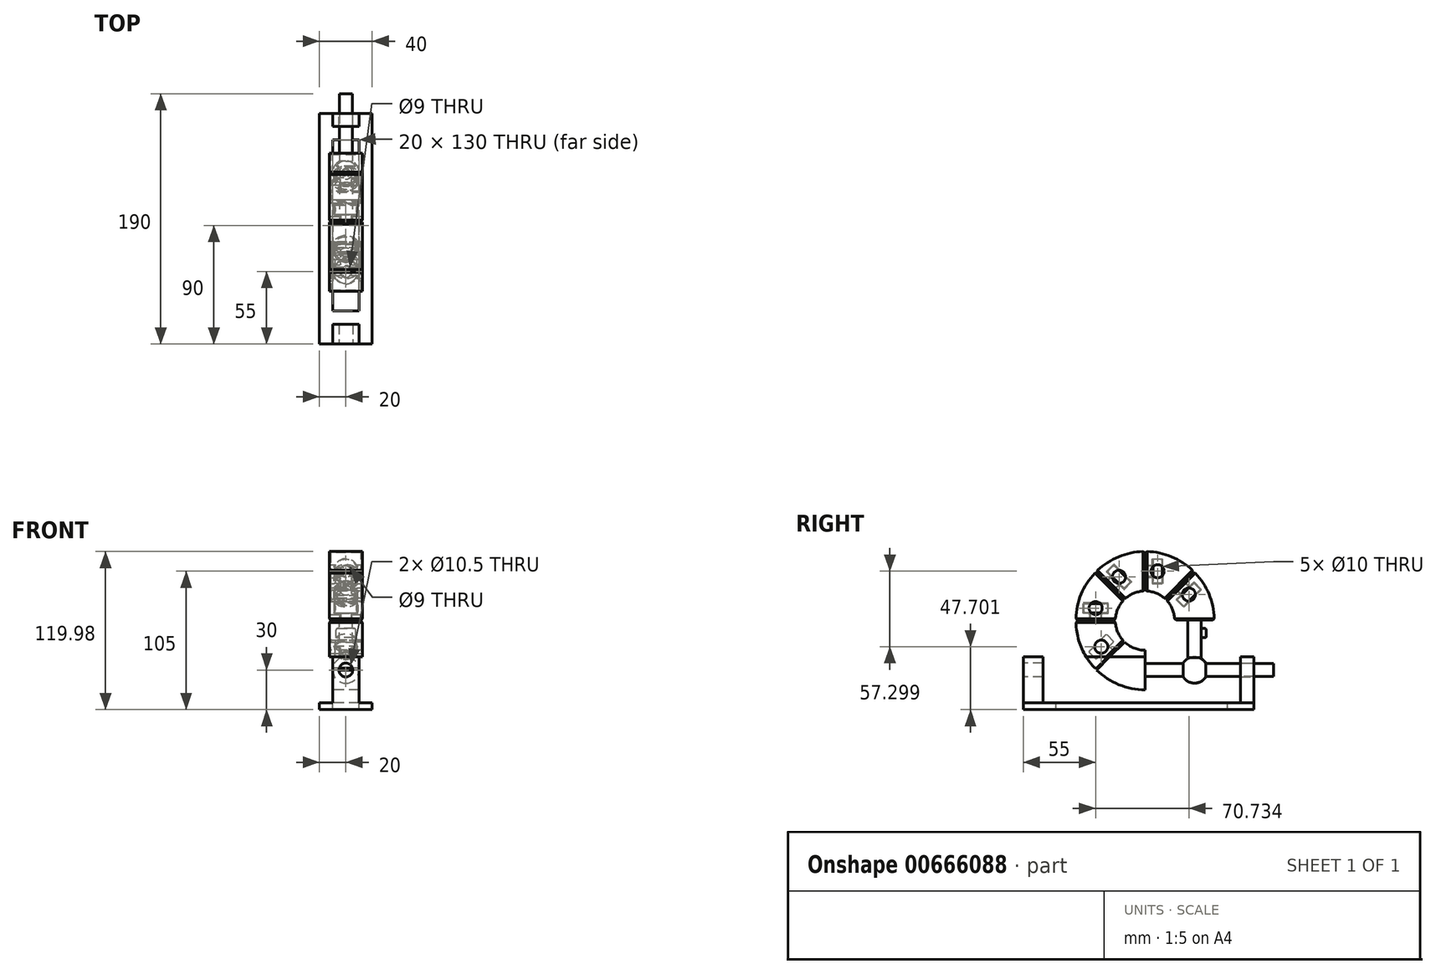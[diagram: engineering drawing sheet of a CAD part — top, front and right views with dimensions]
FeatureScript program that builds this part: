
annotation { "Feature Type Name" : "Feature", "Feature Type Description" : "" }
export const myFeature = defineFeature(function(context is Context, id is Id, definition is map)
    precondition{}
    {
        {
            var Q0;
            Q0=qCreatedBy(makeId("Right.planeOp"),FACE);
            var sketch = newSketch(context, id + "F0", { "sketchPlane" : qUnion([Q0])});
            skLineSegment(sketch, "E0", {"start": v(0, 30) * mm, "end": v(0, 0) * mm});
            skArc(sketch, "E1", {"start": v(-37.12, 15.38) * mm, "mid": v(-20.1, 4) * mm, "end": v(0, 0) * mm});
            skArc(sketch, "E2", {"start": v(0, 30) * mm, "mid": v(-8.61, 31.71) * mm, "end": v(-15.9, 36.6) * mm});
            skLineSegment(sketch, "E3", {"start": v(-15.9, 36.6) * mm, "end": v(-37.12, 15.38) * mm, "construction": true});
            skLineSegment(sketch, "E4", {"start": v(-23.33, 28.46) * mm, "end": v(-27.93, 33.05) * mm});
            skLineSegment(sketch, "E5", {"start": v(-33.59, 27.4) * mm, "end": v(-29, 22.8) * mm});
            skLineSegment(sketch, "E6", {"start": v(-33.59, 27.4) * mm, "end": v(-36.42, 24.57) * mm});
            skLineSegment(sketch, "E7", {"start": v(-37.83, 24.57) * mm, "end": v(-41.37, 28.1) * mm});
            skLineSegment(sketch, "E8", {"start": v(-41.37, 29.52) * mm, "end": v(-30.05, 40.83) * mm});
            skLineSegment(sketch, "E9", {"start": v(-28.64, 40.83) * mm, "end": v(-25.1, 37.3) * mm});
            skLineSegment(sketch, "E10", {"start": v(-25.1, 35.88) * mm, "end": v(-27.93, 33.05) * mm});
            skLineSegment(sketch, "E11", {"start": v(-26.52, 25.98) * mm, "end": v(-36.06, 35.53) * mm});
            skArc(sketch, "E12.MirrorCS", {"start": v(-22.5, 52.5) * mm, "mid": v(-20.79, 43.89) * mm, "end": v(-15.9, 36.6) * mm});
            skLineSegment(sketch, "E13.MirrorCS", {"start": v(-22.5, 52.5) * mm, "end": v(-52.5, 52.5) * mm});
            skArc(sketch, "E14.MirrorCS", {"start": v(-37.12, 15.38) * mm, "mid": v(-48.5, 32.4) * mm, "end": v(-52.5, 52.5) * mm});
            skLineSegment(sketch, "E15", {"start": v(-16.26, 36.95) * mm, "end": v(-22.98, 30.23) * mm});
            skLineSegment(sketch, "E16.MirrorCS", {"start": v(-37.48, 15.73) * mm, "end": v(-30.76, 22.45) * mm});
            skLineSegment(sketch, "E17", {"start": v(-36.77, 15.02) * mm, "end": v(-15.55, 36.24) * mm});
            skLineSegment(sketch, "E18", {"start": v(-30.76, 23.86) * mm, "end": v(-32.88, 25.98) * mm});
            skLineSegment(sketch, "E19", {"start": v(-34.3, 25.98) * mm, "end": v(-37.12, 23.16) * mm});
            skLineSegment(sketch, "E20", {"start": v(-37.12, 23.16) * mm, "end": v(-42.78, 28.81) * mm});
            skLineSegment(sketch, "E21", {"start": v(-42.78, 28.81) * mm, "end": v(-29.34, 42.25) * mm});
            skLineSegment(sketch, "E22", {"start": v(-29.34, 42.25) * mm, "end": v(-23.69, 36.6) * mm});
            skLineSegment(sketch, "E23", {"start": v(-23.69, 36.6) * mm, "end": v(-26.52, 33.76) * mm});
            skLineSegment(sketch, "E24", {"start": v(-26.52, 32.35) * mm, "end": v(-24.4, 30.23) * mm});
            skLineSegment(sketch, "E25", {"start": v(0, 52.5) * mm, "end": v(-51.67, 31.1) * mm, "construction": true});
            skArc(sketch, "E26.1.21", {"start": v(-16.26, 36.95) * mm, "mid": v(-20.88, 44.12) * mm, "end": v(-22.5, 52.5) * mm});
            skPoint(sketch, "E27.orphan", {"position": v(-23.69, 28.81) * mm});
            skPoint(sketch, "E28.orphan", {"position": v(-29.34, 23.16) * mm});
            skLineSegment(sketch, "E29.1.0", {"start": v(-42, 54) * mm, "end": v(-42, 57) * mm});
            skLineSegment(sketch, "E29.1.1", {"start": v(-43, 58) * mm, "end": v(-47, 58) * mm});
            skLineSegment(sketch, "E29.1.2", {"start": v(-47, 58) * mm, "end": v(-47, 66) * mm});
            skLineSegment(sketch, "E29.1.3", {"start": v(-47, 66) * mm, "end": v(-28, 66) * mm});
            skLineSegment(sketch, "E29.1.4", {"start": v(-28, 66) * mm, "end": v(-28, 58) * mm});
            skLineSegment(sketch, "E29.1.5", {"start": v(-28, 58) * mm, "end": v(-32, 58) * mm});
            skLineSegment(sketch, "E29.1.6", {"start": v(-33, 57) * mm, "end": v(-33, 54) * mm});
            skLineSegment(sketch, "E29.1.7", {"start": v(-22.5, 53) * mm, "end": v(-32, 53) * mm});
            skLineSegment(sketch, "E29.1.8", {"start": v(-52.5, 53) * mm, "end": v(-43, 53) * mm});
            skArc(sketch, "E29.1.9", {"start": v(-52.5, 52.5) * mm, "mid": v(-48.5, 72.6) * mm, "end": v(-37.12, 89.62) * mm});
            skArc(sketch, "E29.1.10", {"start": v(-22.5, 53) * mm, "mid": v(-20.7, 61.34) * mm, "end": v(-15.9, 68.4) * mm});
            skLineSegment(sketch, "E29.1.11", {"start": v(-52.5, 52) * mm, "end": v(-22.5, 52) * mm});
            skLineSegment(sketch, "E29.1.12", {"start": v(-15.9, 68.4) * mm, "end": v(-37.12, 89.62) * mm});
            skLineSegment(sketch, "E29.1.13", {"start": v(-28.5, 64.5) * mm, "end": v(-28.5, 59.5) * mm});
            skLineSegment(sketch, "E29.1.14", {"start": v(-45.5, 65.5) * mm, "end": v(-29.5, 65.5) * mm});
            skLineSegment(sketch, "E29.1.15", {"start": v(-46.5, 59.5) * mm, "end": v(-46.5, 64.5) * mm});
            skLineSegment(sketch, "E29.1.16", {"start": v(-41.5, 58.5) * mm, "end": v(-45.5, 58.5) * mm});
            skLineSegment(sketch, "E29.1.17", {"start": v(-41.5, 58.5) * mm, "end": v(-41.5, 52) * mm});
            skLineSegment(sketch, "E29.1.18", {"start": v(-33.5, 52) * mm, "end": v(-33.5, 58.5) * mm});
            skLineSegment(sketch, "E29.1.19", {"start": v(-29.5, 58.5) * mm, "end": v(-33.5, 58.5) * mm});
            skLineSegment(sketch, "E29.2.0", {"start": v(-29.34, 82.55) * mm, "end": v(-25.8, 86.09) * mm});
            skLineSegment(sketch, "E29.2.1", {"start": v(-25.8, 86.09) * mm, "end": v(-29.34, 89.62) * mm});
            skLineSegment(sketch, "E29.2.2", {"start": v(-29.34, 89.62) * mm, "end": v(-23.69, 95.28) * mm});
            skLineSegment(sketch, "E29.2.3", {"start": v(-23.69, 95.28) * mm, "end": v(-10.25, 81.84) * mm});
            skLineSegment(sketch, "E29.2.4", {"start": v(-10.25, 81.84) * mm, "end": v(-15.9, 76.19) * mm});
            skLineSegment(sketch, "E29.2.5", {"start": v(-15.9, 76.19) * mm, "end": v(-19.45, 79.72) * mm});
            skLineSegment(sketch, "E29.2.6", {"start": v(-19.45, 79.72) * mm, "end": v(-22.98, 76.19) * mm});
            skLineSegment(sketch, "E29.2.7", {"start": v(-15.55, 68.76) * mm, "end": v(-22.98, 76.19) * mm});
            skLineSegment(sketch, "E29.2.8", {"start": v(-36.77, 89.98) * mm, "end": v(-29.34, 82.55) * mm});
            skArc(sketch, "E29.2.9", {"start": v(-37.12, 89.62) * mm, "mid": v(-20.1, 101) * mm, "end": v(0, 105) * mm});
            skArc(sketch, "E29.2.10", {"start": v(-15.55, 68.76) * mm, "mid": v(-8.38, 73.38) * mm, "end": v(0, 75) * mm});
            skLineSegment(sketch, "E29.2.11", {"start": v(-37.48, 89.27) * mm, "end": v(-16.26, 68.05) * mm});
            skLineSegment(sketch, "E29.2.12", {"start": v(0, 75) * mm, "end": v(0, 105) * mm});
            skLineSegment(sketch, "E29.2.13", {"start": v(-10.96, 81.84) * mm, "end": v(-15.9, 76.9) * mm});
            skLineSegment(sketch, "E29.2.14", {"start": v(-23.69, 94.57) * mm, "end": v(-10.96, 81.84) * mm});
            skLineSegment(sketch, "E29.2.15", {"start": v(-28.64, 89.62) * mm, "end": v(-23.69, 94.57) * mm});
            skLineSegment(sketch, "E29.2.16", {"start": v(-25.1, 86.09) * mm, "end": v(-28.64, 89.62) * mm});
            skLineSegment(sketch, "E29.2.17", {"start": v(-25.1, 86.09) * mm, "end": v(-29.7, 81.5) * mm});
            skLineSegment(sketch, "E29.2.18", {"start": v(-24.04, 75.83) * mm, "end": v(-19.45, 80.43) * mm});
            skLineSegment(sketch, "E29.2.19", {"start": v(-15.9, 76.9) * mm, "end": v(-19.45, 80.43) * mm});
            skLineSegment(sketch, "E29.3.0", {"start": v(0.5, 94.5) * mm, "end": v(5.5, 94.5) * mm});
            skLineSegment(sketch, "E29.3.1", {"start": v(5.5, 94.5) * mm, "end": v(5.5, 99.5) * mm});
            skLineSegment(sketch, "E29.3.2", {"start": v(5.5, 99.5) * mm, "end": v(13.5, 99.5) * mm});
            skLineSegment(sketch, "E29.3.3", {"start": v(13.5, 99.5) * mm, "end": v(13.5, 80.5) * mm});
            skLineSegment(sketch, "E29.3.4", {"start": v(13.5, 80.5) * mm, "end": v(5.5, 80.5) * mm});
            skLineSegment(sketch, "E29.3.5", {"start": v(5.5, 80.5) * mm, "end": v(5.5, 85.5) * mm});
            skLineSegment(sketch, "E29.3.6", {"start": v(5.5, 85.5) * mm, "end": v(0.5, 85.5) * mm});
            skLineSegment(sketch, "E29.3.7", {"start": v(0.5, 75) * mm, "end": v(0.5, 85.5) * mm});
            skLineSegment(sketch, "E29.3.8", {"start": v(0.5, 105) * mm, "end": v(0.5, 94.5) * mm});
            skArc(sketch, "E29.3.9", {"start": v(0, 105) * mm, "mid": v(20.1, 101) * mm, "end": v(37.12, 89.62) * mm});
            skArc(sketch, "E29.3.10", {"start": v(0.5, 75) * mm, "mid": v(8.84, 73.2) * mm, "end": v(15.9, 68.4) * mm});
            skLineSegment(sketch, "E29.3.11", {"start": v(-0.5, 105) * mm, "end": v(-0.5, 75) * mm});
            skLineSegment(sketch, "E29.3.12", {"start": v(15.9, 68.4) * mm, "end": v(37.12, 89.62) * mm});
            skLineSegment(sketch, "E29.3.13", {"start": v(13, 81) * mm, "end": v(6, 81) * mm});
            skLineSegment(sketch, "E29.3.14", {"start": v(13, 99) * mm, "end": v(13, 81) * mm});
            skLineSegment(sketch, "E29.3.15", {"start": v(6, 99) * mm, "end": v(13, 99) * mm});
            skLineSegment(sketch, "E29.3.16", {"start": v(6, 94) * mm, "end": v(6, 99) * mm});
            skLineSegment(sketch, "E29.3.17", {"start": v(6, 94) * mm, "end": v(-0.5, 94) * mm});
            skLineSegment(sketch, "E29.3.18", {"start": v(-0.5, 86) * mm, "end": v(6, 86) * mm});
            skLineSegment(sketch, "E29.3.19", {"start": v(6, 81) * mm, "end": v(6, 86) * mm});
            skLineSegment(sketch, "E29.4.0", {"start": v(30.05, 81.84) * mm, "end": v(33.59, 78.3) * mm});
            skLineSegment(sketch, "E29.4.1", {"start": v(33.59, 78.3) * mm, "end": v(37.12, 81.84) * mm});
            skLineSegment(sketch, "E29.4.2", {"start": v(37.12, 81.84) * mm, "end": v(42.78, 76.19) * mm});
            skLineSegment(sketch, "E29.4.3", {"start": v(42.78, 76.19) * mm, "end": v(29.34, 62.75) * mm});
            skLineSegment(sketch, "E29.4.4", {"start": v(29.34, 62.75) * mm, "end": v(23.69, 68.4) * mm});
            skLineSegment(sketch, "E29.4.5", {"start": v(23.69, 68.4) * mm, "end": v(27.22, 71.95) * mm});
            skLineSegment(sketch, "E29.4.6", {"start": v(27.22, 71.95) * mm, "end": v(23.69, 75.48) * mm});
            skLineSegment(sketch, "E29.4.7", {"start": v(16.26, 68.05) * mm, "end": v(23.69, 75.48) * mm});
            skLineSegment(sketch, "E29.4.8", {"start": v(37.48, 89.27) * mm, "end": v(30.05, 81.84) * mm});
            skArc(sketch, "E29.4.9", {"start": v(37.12, 89.62) * mm, "mid": v(48.5, 72.6) * mm, "end": v(52.5, 52.5) * mm});
            skArc(sketch, "E29.4.10", {"start": v(16.26, 68.05) * mm, "mid": v(20.88, 60.88) * mm, "end": v(22.5, 52.5) * mm});
            skLineSegment(sketch, "E29.4.11", {"start": v(36.77, 89.98) * mm, "end": v(15.55, 68.76) * mm});
            skLineSegment(sketch, "E29.4.12", {"start": v(22.5, 52.5) * mm, "end": v(52.5, 52.5) * mm});
            skLineSegment(sketch, "E29.4.13", {"start": v(29.34, 63.46) * mm, "end": v(24.4, 68.4) * mm});
            skLineSegment(sketch, "E29.4.14", {"start": v(42.07, 76.19) * mm, "end": v(29.34, 63.46) * mm});
            skLineSegment(sketch, "E29.4.15", {"start": v(37.12, 81.14) * mm, "end": v(42.07, 76.19) * mm});
            skLineSegment(sketch, "E29.4.16", {"start": v(33.59, 77.6) * mm, "end": v(37.12, 81.14) * mm});
            skLineSegment(sketch, "E29.4.17", {"start": v(33.59, 77.6) * mm, "end": v(29, 82.2) * mm});
            skLineSegment(sketch, "E29.4.18", {"start": v(23.33, 76.54) * mm, "end": v(27.93, 71.95) * mm});
            skLineSegment(sketch, "E29.4.19", {"start": v(24.4, 68.4) * mm, "end": v(27.93, 71.95) * mm});
            skLineSegment(sketch, "E29.anchor1", {"start": v(0, 52.5) * mm, "end": v(-33.59, 26.7) * mm, "construction": true});
            skLineSegment(sketch, "E29.anchor2", {"start": v(0, 52.5) * mm, "end": v(33.59, 78.3) * mm, "construction": true});
            skLineSegment(sketch, "E30", {"start": v(0, 20) * mm, "end": v(40, 20) * mm});
            skLineSegment(sketch, "E31", {"start": v(40, 20) * mm, "end": v(40, 10) * mm});
            skLineSegment(sketch, "E32", {"start": v(40, 10) * mm, "end": v(0, 10) * mm});
            skLineSegment(sketch, "E33", {"start": v(32.5, 53) * mm, "end": v(32.5, 25) * mm});
            skLineSegment(sketch, "E34", {"start": v(32.5, 25) * mm, "end": v(42.5, 25) * mm, "construction": true});
            skLineSegment(sketch, "E35", {"start": v(42.5, 25) * mm, "end": v(42.5, 53) * mm});
            skLineSegment(sketch, "E36", {"start": v(0, 15) * mm, "end": v(40, 15) * mm});
            skPoint(sketch, "E36.endSnap0", {"position": v(0, 15) * mm});
            skLineSegment(sketch, "E37", {"start": v(37.5, 53) * mm, "end": v(37.5, 15) * mm});
            skLineSegment(sketch, "E38", {"start": v(-26.52, 25.98) * mm, "end": v(-26.16, 25.63) * mm});
            skLineSegment(sketch, "E39", {"start": v(-24.04, 29.17) * mm, "end": v(-29.7, 23.5) * mm});
            skLineSegment(sketch, "E40", {"start": v(-37.5, 52) * mm, "end": v(-37.5, 65.5) * mm});
            skPoint(sketch, "E41.visualSharp", {"position": v(-42.07, 28.81) * mm});
            skArc(sketch, "E41.filletArc", {"start": v(-41.37, 29.52) * mm, "mid": v(-41.66, 28.81) * mm, "end": v(-41.37, 28.1) * mm});
            skPoint(sketch, "E42.visualSharp", {"position": v(-29.34, 41.54) * mm});
            skArc(sketch, "E42.filletArc", {"start": v(-28.64, 40.83) * mm, "mid": v(-29.34, 41.13) * mm, "end": v(-30.05, 40.83) * mm});
            skPoint(sketch, "E43.visualSharp", {"position": v(-24.4, 36.6) * mm});
            skArc(sketch, "E43.filletArc", {"start": v(-25.1, 35.88) * mm, "mid": v(-24.8, 36.6) * mm, "end": v(-25.1, 37.3) * mm});
            skPoint(sketch, "E44.visualSharp", {"position": v(-37.12, 23.86) * mm});
            skArc(sketch, "E44.filletArc", {"start": v(-37.83, 24.57) * mm, "mid": v(-37.12, 24.28) * mm, "end": v(-36.42, 24.57) * mm});
            skPoint(sketch, "E45.visualSharp", {"position": v(-27.22, 33.05) * mm});
            skArc(sketch, "E45.filletArc", {"start": v(-26.52, 33.76) * mm, "mid": v(-26.8, 33.05) * mm, "end": v(-26.52, 32.35) * mm});
            skPoint(sketch, "E46.visualSharp", {"position": v(-33.59, 26.7) * mm});
            skArc(sketch, "E46.filletArc", {"start": v(-32.88, 25.98) * mm, "mid": v(-33.59, 26.28) * mm, "end": v(-34.3, 25.98) * mm});
            skPoint(sketch, "E47.visualSharp", {"position": v(-46.5, 65.5) * mm});
            skArc(sketch, "E47.filletArc", {"start": v(-45.5, 65.5) * mm, "mid": v(-46.2, 65.2) * mm, "end": v(-46.5, 64.5) * mm});
            skPoint(sketch, "E48.visualSharp", {"position": v(-28.5, 65.5) * mm});
            skArc(sketch, "E48.filletArc", {"start": v(-28.5, 64.5) * mm, "mid": v(-28.8, 65.2) * mm, "end": v(-29.5, 65.5) * mm});
            skPoint(sketch, "E49.visualSharp", {"position": v(-28.5, 58.5) * mm});
            skArc(sketch, "E49.filletArc", {"start": v(-29.5, 58.5) * mm, "mid": v(-28.8, 58.8) * mm, "end": v(-28.5, 59.5) * mm});
            skPoint(sketch, "E50.visualSharp", {"position": v(-33, 58) * mm});
            skArc(sketch, "E50.filletArc", {"start": v(-32, 58) * mm, "mid": v(-32.7, 57.7) * mm, "end": v(-33, 57) * mm});
            skPoint(sketch, "E51.visualSharp", {"position": v(-42, 58) * mm});
            skArc(sketch, "E51.filletArc", {"start": v(-42, 57) * mm, "mid": v(-42.3, 57.7) * mm, "end": v(-43, 58) * mm});
            skPoint(sketch, "E52.visualSharp", {"position": v(-46.5, 58.5) * mm});
            skArc(sketch, "E52.filletArc", {"start": v(-46.5, 59.5) * mm, "mid": v(-46.2, 58.8) * mm, "end": v(-45.5, 58.5) * mm});
            skLineSegment(sketch, "E53", {"start": v(22.5, 53) * mm, "end": v(52.5, 53) * mm});
            skPoint(sketch, "E54.visualSharp", {"position": v(-42, 53) * mm});
            skArc(sketch, "E54.filletArc", {"start": v(-43, 53) * mm, "mid": v(-42.3, 53.3) * mm, "end": v(-42, 54) * mm});
            skPoint(sketch, "E55.visualSharp", {"position": v(-33, 53) * mm});
            skArc(sketch, "E55.filletArc", {"start": v(-33, 54) * mm, "mid": v(-32.7, 53.3) * mm, "end": v(-32, 53) * mm});
            skPoint(sketch, "E56.visualSharp", {"position": v(-30.05, 23.16) * mm});
            skArc(sketch, "E56.filletArc", {"start": v(-30.76, 22.45) * mm, "mid": v(-30.47, 23.16) * mm, "end": v(-30.76, 23.86) * mm});
            skPoint(sketch, "E57.visualSharp", {"position": v(-23.69, 29.52) * mm});
            skArc(sketch, "E57.filletArc", {"start": v(-24.4, 30.23) * mm, "mid": v(-23.69, 29.93) * mm, "end": v(-22.98, 30.23) * mm});
            skLineSegment(sketch, "E58", {"start": v(-30.76, 22.45) * mm, "end": v(-29.7, 23.5) * mm});
            skLineSegment(sketch, "E59", {"start": v(-24.04, 29.17) * mm, "end": v(-22.98, 30.23) * mm});
            skLineSegment(sketch, "E60", {"start": v(42.5, 52.5) * mm, "end": v(52.5, 52.5) * mm});
            skLineSegment(sketch, "E61", {"start": v(0, 20) * mm, "end": v(0, 30) * mm});
            skLineSegment(sketch, "E62", {"start": v(0, 10) * mm, "end": v(0, 0) * mm});
            skLineSegment(sketch, "E63", {"start": v(37.5, 15) * mm, "end": v(40, 15) * mm, "construction": true});
            skArc(sketch, "E64", {"start": v(37.5, 25) * mm, "mid": v(47.5, 15) * mm, "end": v(37.5, 5) * mm});
            skLineSegment(sketch, "E65", {"start": v(37.5, 15) * mm, "end": v(37.5, 5) * mm});
            skLineSegment(sketch, "E66", {"start": v(0, 30) * mm, "end": v(40, 30) * mm});
            skLineSegment(sketch, "E67", {"start": v(40, 30) * mm, "end": v(40, 20) * mm});
            skLineSegment(sketch, "E68", {"start": v(32.5, 25) * mm, "end": v(32.5, 24.5) * mm});
            skLineSegment(sketch, "E69", {"start": v(32.5, 24.5) * mm, "end": v(42.5, 24.5) * mm});
            skLineSegment(sketch, "E70", {"start": v(42.5, 24.5) * mm, "end": v(42.5, 25) * mm});
            skLineSegment(sketch, "E71", {"start": v(52.5, 52.5) * mm, "end": v(52.5, 28.52) * mm});
            skLineSegment(sketch, "E72", {"start": v(52.5, 28.52) * mm, "end": v(22.5, 28.52) * mm});
            skLineSegment(sketch, "E73", {"start": v(22.5, 28.52) * mm, "end": v(22.5, 52.5) * mm});
            skPoint(sketch, "E74.orphan", {"position": v(37.5, 52.5) * mm});
            skSolve(sketch);
        }
        {
            var Q0;
            {var subQ1=sQuery(id+"F0.wireOp",EDGE,"E0");var subQ9=sQuery(id+"F0.wireOp",EDGE,"E2");var subQ10=makeQuery(id+"F0.imprint","INTERSECT",VERTEX,{"derivedFrom":[subQ1,subQ9]});Q0=makeQuery(id+"F0.imprint","IMPRINT",FACE,{"disambiguationData":[TD([[makeQuery(id+"F0.imprint","IMPRINT",EDGE,{"disambiguationData":[TD([[subQ10,-1.0]])],"derivedFrom":subQ1}),-1.0]])]});}
            extrude(context, id + "F1", {"entities" : qUnion([Q0]), "endBound" : BoundingType.SYMMETRIC, "depth" : 25 * mm, "offsetDistance" : 25 * mm, "hasSecondDirection" : true, "secondDirectionOppositeDirection" : true, "secondDirectionDepth" : 20 * mm});
        }
        {
            var Q0;
            {var subQ2=sQuery(id+"F0.wireOp",EDGE,"E4");Q0=makeQuery(id+"F0.imprint","IMPRINT",FACE,{"disambiguationData":[TD([[makeQuery(id+"F0.imprint","IMPRINT",EDGE,{"derivedFrom":subQ2}),1.0]])]});}
            var Q1;
            {var subQ1=sQuery(id+"F0.wireOp",EDGE,"E9");Q1=makeQuery(id+"F0.imprint","IMPRINT",FACE,{"disambiguationData":[TD([[makeQuery(id+"F0.imprint","IMPRINT",EDGE,{"derivedFrom":subQ1}),-1.0]])]});}
            var Q2;
            Q2=sQuery(id+"F0.wireOp",EDGE,"E11");
            revolve(context, id + "F2", {"operationType" : NewBodyOperationType.ADD, "entities" : qUnion([Q0, Q1]), "axis" : qUnion([Q2]), "revolveType" : RevolveType.FULL});
        }
        {
            var Q0;
            {var subQ0=sQuery(id+"F0.wireOp",EDGE,"E30");Q0=makeQuery(id+"F0.imprint","IMPRINT",FACE,{"disambiguationData":[TD([[makeQuery(id+"F0.imprint","IMPRINT",EDGE,{"derivedFrom":subQ0}),-1.0]])]});}
            var Q1;
            Q1=sQuery(id+"F0.wireOp",EDGE,"E36");
            revolve(context, id + "F3", {"operationType" : NewBodyOperationType.ADD, "entities" : qUnion([Q0]), "axis" : qUnion([Q1]), "revolveType" : RevolveType.FULL});
        }
        {
            var Q0;
            {var subQ7=sQuery(id+"F0.wireOp",EDGE,"E15");Q0=makeQuery(id+"F0.imprint","IMPRINT",FACE,{"disambiguationData":[TD([[makeQuery(id+"F0.imprint","IMPRINT",EDGE,{"derivedFrom":subQ7}),-1.0]])]});}
            var Q1;
            {var subQ2=sQuery(id+"F0.wireOp",EDGE,"E9");Q1=makeQuery(id+"F0.imprint","IMPRINT",FACE,{"disambiguationData":[TD([[makeQuery(id+"F0.imprint","IMPRINT",EDGE,{"derivedFrom":subQ2}),1.0]])]});}
            var Q2;
            {var subQ1=sQuery(id+"F0.wireOp",EDGE,"E9");Q2=makeQuery(id+"F0.imprint","IMPRINT",FACE,{"disambiguationData":[TD([[makeQuery(id+"F0.imprint","IMPRINT",EDGE,{"derivedFrom":subQ1}),-1.0]])]});}
            var Q3;
            {var subQ4=sQuery(id+"F0.wireOp",EDGE,"E6");Q3=makeQuery(id+"F0.imprint","IMPRINT",FACE,{"disambiguationData":[TD([[makeQuery(id+"F0.imprint","IMPRINT",EDGE,{"derivedFrom":subQ4}),-1.0]])]});}
            var Q4;
            {var subQ7=sQuery(id+"F0.wireOp",EDGE,"E6");Q4=makeQuery(id+"F0.imprint","IMPRINT",FACE,{"disambiguationData":[TD([[makeQuery(id+"F0.imprint","IMPRINT",EDGE,{"derivedFrom":subQ7}),1.0]])]});}
            extrude(context, id + "F4", {"entities" : qUnion([Q0, Q1, Q2, Q3, Q4]), "endBound" : BoundingType.SYMMETRIC, "depth" : 25 * mm, "offsetDistance" : 25 * mm, "hasSecondDirection" : true, "secondDirectionOppositeDirection" : true, "secondDirectionDepth" : 20 * mm});
        }
        {
            var Q0;
            Q0=makeQuery(id+"F4.opExtrude","CAP_FACE",FACE,{"disambiguationData":[OSD([sQuery(id+"F0.wireOp",EDGE,"E14.MirrorCS"),sQuery(id+"F0.wireOp",EDGE,"E15"),sQuery(id+"F0.wireOp",EDGE,"E16.MirrorCS"),sQuery(id+"F0.wireOp",EDGE,"E26.1.21"),sQuery(id+"F0.wireOp",EDGE,"E29.1.11"),sQuery(id+"F0.wireOp",EDGE,"E39")])],"isStart":false});
            var sketch = newSketch(context, id + "F5", { "sketchPlane" : qUnion([Q0])});
            skPoint(sketch, "E75", {"position": v(-33.23, 32.7) * mm});
            skSolve(sketch);
        }
        {
            var Q0;
            Q0=sQuery(id+"F5.wireOp",VERTEX,"E75");
            var Q1;
            Q1=makeQuery(id+"F4.opExtrude","SWEPT_BODY",BODY,{"disambiguationData":[OSD([sQuery(id+"F0.wireOp",EDGE,"E14.MirrorCS"),sQuery(id+"F0.wireOp",EDGE,"E15"),sQuery(id+"F0.wireOp",EDGE,"E16.MirrorCS"),sQuery(id+"F0.wireOp",EDGE,"E26.1.21"),sQuery(id+"F0.wireOp",EDGE,"E29.1.11"),sQuery(id+"F0.wireOp",EDGE,"E39")])]});
            hole(context, id + "F6", {"style" : HoleStyle.SIMPLE, "endStyle" : HoleEndStyle.THROUGH, "holeDiameter" : 10 * mm, "majorDiameter" : 5 * mm, "isTappedThrough" : true, "tappedDepth" : 12 * mm, "tapClearance" : 3, "locations" : qUnion([Q0]), "scope" : qUnion([Q1])});
        }
        {
            var Q0;
            Q0=sQuery(id+"F0.wireOp",EDGE,"E7");
            cPoint(context, id + "F7", {"entities" : qUnion([Q0]), "parameter" : 0.5});
        }
        {
            var Q0;
            Q0=qCreatedBy(id+"F7",VERTEX);
            var Q1;
            Q1=sQuery(id+"F0.wireOp",EDGE,"E21");
            cPlane(context, id + "F8", {"entities" : qUnion([Q0, Q1]), "cplaneType" : CPlaneType.LINE_POINT, "offset" : 25 * mm, "width" : 150 * mm, "height" : 150 * mm});
        }
        {
            var Q0;
            Q0=qCreatedBy(id+"F8.planeOp",FACE);
            var sketch = newSketch(context, id + "F9", { "sketchPlane" : qUnion([Q0])});
            skPoint(sketch, "E76", {"position": v(0, -35.26) * mm});
            skSolve(sketch);
        }
        {
            var Q0;
            Q0=makeQuery(id+"F4.opExtrude","CAP_EDGE",EDGE,{"disambiguationData":[OSD([sQuery(id+"F0.wireOp",EDGE,"E15"),sQuery(id+"F0.wireOp",EDGE,"E16.MirrorCS"),sQuery(id+"F0.wireOp",EDGE,"E39")])],"isStart":true});
            var Q1;
            Q1=makeQuery(id+"F4.opExtrude","SWEPT_EDGE",EDGE,{"disambiguationData":[OSD([sQuery(id+"F0.wireOp",EDGE,"E15"),sQuery(id+"F0.wireOp",EDGE,"E26.1.21")])]});
            var Q2;
            Q2=makeQuery(id+"F4.opExtrude","CAP_EDGE",EDGE,{"disambiguationData":[OSD([sQuery(id+"F0.wireOp",EDGE,"E15"),sQuery(id+"F0.wireOp",EDGE,"E16.MirrorCS"),sQuery(id+"F0.wireOp",EDGE,"E39")])],"isStart":false});
            var Q3;
            Q3=makeQuery(id+"F4.opExtrude","SWEPT_EDGE",EDGE,{"disambiguationData":[OSD([sQuery(id+"F0.wireOp",EDGE,"E14.MirrorCS"),sQuery(id+"F0.wireOp",EDGE,"E16.MirrorCS")])]});
            var Q4;
            Q4=makeQuery(id+"F4.opExtrude","CAP_EDGE",EDGE,{"disambiguationData":[OSD([sQuery(id+"F0.wireOp",EDGE,"E29.1.11")])],"isStart":true});
            var Q5;
            Q5=makeQuery(id+"F4.opExtrude","SWEPT_EDGE",EDGE,{"disambiguationData":[OSD([sQuery(id+"F0.wireOp",EDGE,"E14.MirrorCS"),sQuery(id+"F0.wireOp",EDGE,"E29.1.11")])]});
            var Q6;
            Q6=makeQuery(id+"F4.opExtrude","CAP_EDGE",EDGE,{"disambiguationData":[OSD([sQuery(id+"F0.wireOp",EDGE,"E29.1.11")])],"isStart":false});
            var Q7;
            Q7=makeQuery(id+"F4.opExtrude","SWEPT_EDGE",EDGE,{"disambiguationData":[OSD([sQuery(id+"F0.wireOp",EDGE,"E26.1.21"),sQuery(id+"F0.wireOp",EDGE,"E29.1.11")])]});
            chamfer(context, id + "F10", {"entities" : qUnion([Q0, Q1, Q2, Q3, Q4, Q5, Q6, Q7]), "width" : 1 * mm, "tangentPropagation" : true});
        }
        {
            var Q0;
            {var subQ1=sQuery(id+"F0.wireOp",EDGE,"E29.1.13");Q0=makeQuery(id+"F0.imprint","IMPRINT",FACE,{"disambiguationData":[TD([[makeQuery(id+"F0.imprint","IMPRINT",EDGE,{"derivedFrom":subQ1}),-1.0]])]});}
            var Q1;
            {var subQ0=sQuery(id+"F0.wireOp",EDGE,"E29.1.18");var subQ1=sQuery(id+"F0.wireOp",EDGE,"E13.MirrorCS");var subQ2=makeQuery(id+"F0.imprint","INTERSECT",VERTEX,{"derivedFrom":[subQ1,subQ0]});Q1=makeQuery(id+"F0.imprint","IMPRINT",FACE,{"disambiguationData":[TD([[makeQuery(id+"F0.imprint","IMPRINT",EDGE,{"disambiguationData":[TD([[subQ2,-1.0]])],"derivedFrom":subQ1}),1.0]])]});}
            var Q2;
            Q2=sQuery(id+"F0.wireOp",EDGE,"E40");
            revolve(context, id + "F11", {"operationType" : NewBodyOperationType.ADD, "entities" : qUnion([Q0, Q1]), "axis" : qUnion([Q2]), "revolveType" : RevolveType.FULL});
        }
        {
            var Q0;
            {var subQ1=sQuery(id+"F0.wireOp",EDGE,"E9");Q0=makeQuery(id+"F0.imprint","IMPRINT",FACE,{"disambiguationData":[TD([[makeQuery(id+"F0.imprint","IMPRINT",EDGE,{"derivedFrom":subQ1}),-1.0]])]});}
            var Q1;
            {var subQ2=sQuery(id+"F0.wireOp",EDGE,"E9");Q1=makeQuery(id+"F0.imprint","IMPRINT",FACE,{"disambiguationData":[TD([[makeQuery(id+"F0.imprint","IMPRINT",EDGE,{"derivedFrom":subQ2}),1.0]])]});}
            var Q2;
            Q2=sQuery(id+"F0.wireOp",EDGE,"E11");
            revolve(context, id + "F12", {"operationType" : NewBodyOperationType.REMOVE, "entities" : qUnion([Q0, Q1]), "axis" : qUnion([Q2]), "revolveType" : RevolveType.FULL, "oppositeDirection" : true});
        }
        {
            var Q0;
            Q0=qCreatedBy(makeId("Right.planeOp"),FACE);
            var sketch = newSketch(context, id + "F13", { "sketchPlane" : qUnion([Q0])});
            skLineSegment(sketch, "E77", {"start": v(-28.28, 26.34) * mm, "end": v(-26.87, 24.92) * mm});
            skLineSegment(sketch, "E78", {"start": v(-26.87, 24.92) * mm, "end": v(-25.46, 26.34) * mm});
            skLineSegment(sketch, "E79", {"start": v(-25.46, 26.34) * mm, "end": v(-26.87, 27.75) * mm});
            skLineSegment(sketch, "E80", {"start": v(-26.87, 27.75) * mm, "end": v(-28.28, 26.34) * mm});
            skSolve(sketch);
        }
        {
            var Q0;
            Q0=makeQuery(id+"F4.opExtrude","SWEPT_BODY",BODY,{"disambiguationData":[OSD([sQuery(id+"F0.wireOp",EDGE,"E15"),sQuery(id+"F0.wireOp",EDGE,"E16.MirrorCS"),sQuery(id+"F0.wireOp",EDGE,"E26.1.20"),sQuery(id+"F0.wireOp",EDGE,"E26.1.21"),sQuery(id+"F0.wireOp",EDGE,"E29.1.11"),sQuery(id+"F0.wireOp",EDGE,"E39")])]});
            var Q1;
            Q1=makeQuery(id+"F1.opExtrude","SWEPT_FACE",FACE,{"disambiguationData":[OSD([sQuery(id+"F0.wireOp",EDGE,"E2")])]});
            circularPattern(context, id + "F14", {"entities" : qUnion([Q0]), "axis" : qUnion([Q1]), "angle" : 180 * degree, "instanceCount" : 5, "oppositeDirection" : true, "equalSpace" : true});
        }
        {
            var Q0;
            {var subQ0=sQuery(id+"F0.wireOp",EDGE,"E37");var subQ1=sQuery(id+"F0.wireOp",EDGE,"E29.4.12");var subQ2=makeQuery(id+"F0.imprint","INTERSECT",VERTEX,{"derivedFrom":[subQ1,subQ0]});Q0=makeQuery(id+"F0.imprint","IMPRINT",FACE,{"disambiguationData":[TD([[makeQuery(id+"F0.imprint","IMPRINT",EDGE,{"disambiguationData":[TD([[subQ2,-1.0]])],"derivedFrom":subQ0}),1.0]])]});}
            var Q1;
            {var subQ0=sQuery(id+"F0.wireOp",EDGE,"E33");var subQ1=sQuery(id+"F0.wireOp",EDGE,"E29.4.12");var subQ2=makeQuery(id+"F0.imprint","INTERSECT",VERTEX,{"derivedFrom":[subQ1,subQ0]});Q1=makeQuery(id+"F0.imprint","IMPRINT",FACE,{"disambiguationData":[TD([[makeQuery(id+"F0.imprint","IMPRINT",EDGE,{"disambiguationData":[TD([[subQ2,-1.0]])],"derivedFrom":subQ1}),-1.0]])]});}
            var Q2;
            {var subQ1=sQuery(id+"F0.wireOp",EDGE,"E29.4.12");var subQ3=sQuery(id+"F0.wireOp",EDGE,"E33");var subQ4=makeQuery(id+"F0.imprint","INTERSECT",VERTEX,{"derivedFrom":[subQ1,subQ3]});Q2=makeQuery(id+"F0.imprint","IMPRINT",FACE,{"disambiguationData":[TD([[makeQuery(id+"F0.imprint","IMPRINT",EDGE,{"disambiguationData":[TD([[subQ4,-1.0]])],"derivedFrom":subQ3}),-1.0]])]});}
            var Q3;
            {var subQ0=sQuery(id+"F0.wireOp",EDGE,"E66");var subQ1=sQuery(id+"F0.wireOp",EDGE,"E33");var subQ2=makeQuery(id+"F0.imprint","INTERSECT",VERTEX,{"derivedFrom":[subQ1,subQ0]});Q3=makeQuery(id+"F0.imprint","IMPRINT",FACE,{"disambiguationData":[TD([[makeQuery(id+"F0.imprint","IMPRINT",EDGE,{"disambiguationData":[TD([[subQ2,-1.0]])],"derivedFrom":subQ1}),-1.0]])]});}
            var Q4;
            {var subQ0=sQuery(id+"F0.wireOp",EDGE,"E66");var subQ1=sQuery(id+"F0.wireOp",EDGE,"E33");var subQ2=makeQuery(id+"F0.imprint","INTERSECT",VERTEX,{"derivedFrom":[subQ1,subQ0]});Q4=makeQuery(id+"F0.imprint","IMPRINT",FACE,{"disambiguationData":[TD([[makeQuery(id+"F0.imprint","IMPRINT",EDGE,{"disambiguationData":[TD([[subQ2,-1.0]])],"derivedFrom":subQ1}),1.0]])]});}
            var Q5;
            {var subQ0=sQuery(id+"F0.wireOp",EDGE,"E66");var subQ1=sQuery(id+"F0.wireOp",EDGE,"E37");var subQ2=makeQuery(id+"F0.imprint","INTERSECT",VERTEX,{"derivedFrom":[subQ1,subQ0]});Q5=makeQuery(id+"F0.imprint","IMPRINT",FACE,{"disambiguationData":[TD([[makeQuery(id+"F0.imprint","IMPRINT",EDGE,{"disambiguationData":[TD([[subQ2,-1.0]])],"derivedFrom":subQ1}),1.0]])]});}
            var Q6;
            {var subQ0=sQuery(id+"F0.wireOp",EDGE,"E60");Q6=makeQuery(id+"F0.imprint","IMPRINT",FACE,{"disambiguationData":[TD([[makeQuery(id+"F0.imprint","IMPRINT",EDGE,{"derivedFrom":subQ0}),-1.0]])]});}
            var Q7;
            {var subQ3=sQuery(id+"F0.wireOp",EDGE,"E53");var subQ5=sQuery(id+"F0.wireOp",EDGE,"E33");var subQ6=makeQuery(id+"F0.imprint","INTERSECT",VERTEX,{"derivedFrom":[subQ5,subQ3]});Q7=makeQuery(id+"F0.imprint","IMPRINT",FACE,{"disambiguationData":[TD([[makeQuery(id+"F0.imprint","IMPRINT",EDGE,{"disambiguationData":[TD([[subQ6,-1.0]])],"derivedFrom":subQ5}),-1.0]])]});}
            var Q8;
            {var subQ0=sQuery(id+"F0.wireOp",EDGE,"E33");var subQ1=sQuery(id+"F0.wireOp",EDGE,"E29.4.12");var subQ2=makeQuery(id+"F0.imprint","INTERSECT",VERTEX,{"derivedFrom":[subQ1,subQ0]});Q8=makeQuery(id+"F0.imprint","IMPRINT",FACE,{"disambiguationData":[TD([[makeQuery(id+"F0.imprint","IMPRINT",EDGE,{"disambiguationData":[TD([[subQ2,-1.0]])],"derivedFrom":subQ1}),1.0]])]});}
            var Q9;
            {var subQ3=sQuery(id+"F0.wireOp",EDGE,"E37");var subQ5=sQuery(id+"F0.wireOp",EDGE,"E53");var subQ6=makeQuery(id+"F0.imprint","INTERSECT",VERTEX,{"derivedFrom":[subQ3,subQ5]});Q9=makeQuery(id+"F0.imprint","IMPRINT",FACE,{"disambiguationData":[TD([[makeQuery(id+"F0.imprint","IMPRINT",EDGE,{"disambiguationData":[TD([[subQ6,-1.0]])],"derivedFrom":subQ3}),1.0]])]});}
            var Q10;
            {var subQ0=sQuery(id+"F0.wireOp",EDGE,"E60");Q10=makeQuery(id+"F0.imprint","IMPRINT",FACE,{"disambiguationData":[TD([[makeQuery(id+"F0.imprint","IMPRINT",EDGE,{"derivedFrom":subQ0}),1.0]])]});}
            extrude(context, id + "F15", {"entities" : qUnion([Q0, Q1, Q2, Q3, Q4, Q5, Q6, Q7, Q8, Q9, Q10]), "operationType" : NewBodyOperationType.REMOVE, "endBound" : BoundingType.SYMMETRIC, "oppositeDirection" : true, "depth" : 30 * mm, "offsetDistance" : 25 * mm, "hasSecondDirection" : true, "secondDirectionBound" : SecondDirectionBoundingType.UP_TO_NEXT, "secondDirectionOppositeDirection" : false, "secondDirectionDepth" : 25 * mm});
        }
        {
            var Q0;
            {var subQ0=sQuery(id+"F0.wireOp",EDGE,"E65");Q0=makeQuery(id+"F0.imprint","IMPRINT",FACE,{"disambiguationData":[TD([[makeQuery(id+"F0.imprint","IMPRINT",EDGE,{"derivedFrom":subQ0}),1.0]])]});}
            var Q1;
            {var subQ0=sQuery(id+"F0.wireOp",EDGE,"E64");var subQ1=sQuery(id+"F0.wireOp",EDGE,"E37");var subQ2=makeQuery(id+"F0.imprint","INTERSECT",VERTEX,{"derivedFrom":[subQ1,subQ0]});Q1=makeQuery(id+"F0.imprint","IMPRINT",FACE,{"disambiguationData":[TD([[makeQuery(id+"F0.imprint","IMPRINT",EDGE,{"disambiguationData":[TD([[subQ2,-1.0]])],"derivedFrom":subQ1}),1.0]])]});}
            var Q2;
            {var subQ1=sQuery(id+"F0.wireOp",EDGE,"E30");var subQ3=sQuery(id+"F0.wireOp",EDGE,"E37");var subQ4=makeQuery(id+"F0.imprint","INTERSECT",VERTEX,{"derivedFrom":[subQ1,subQ3]});Q2=makeQuery(id+"F0.imprint","IMPRINT",FACE,{"disambiguationData":[TD([[makeQuery(id+"F0.imprint","IMPRINT",EDGE,{"disambiguationData":[TD([[subQ4,1.0]])],"derivedFrom":subQ3}),1.0]])]});}
            var Q3;
            {var subQ5=sQuery(id+"F0.wireOp",EDGE,"E32");var subQ6=sQuery(id+"F0.wireOp",EDGE,"E31");var subQ7=makeQuery(id+"F0.imprint","INTERSECT",VERTEX,{"derivedFrom":[subQ6,subQ5]});Q3=makeQuery(id+"F0.imprint","IMPRINT",FACE,{"disambiguationData":[TD([[makeQuery(id+"F0.imprint","IMPRINT",EDGE,{"disambiguationData":[TD([[subQ7,1.0]])],"derivedFrom":subQ6}),1.0]])]});}
            var Q4;
            {var subQ1=sQuery(id+"F0.wireOp",EDGE,"E30");var subQ3=sQuery(id+"F0.wireOp",EDGE,"E37");var subQ4=makeQuery(id+"F0.imprint","INTERSECT",VERTEX,{"derivedFrom":[subQ1,subQ3]});Q4=makeQuery(id+"F0.imprint","IMPRINT",FACE,{"disambiguationData":[TD([[makeQuery(id+"F0.imprint","IMPRINT",EDGE,{"disambiguationData":[TD([[subQ4,-1.0]])],"derivedFrom":subQ1}),-1.0]])]});}
            var Q5;
            {var subQ0=sQuery(id+"F0.wireOp",EDGE,"E69");var subQ1=sQuery(id+"F0.wireOp",EDGE,"E64");var subQ2=makeQuery(id+"F0.imprint","INTERSECT",VERTEX,{"derivedFrom":[subQ1,subQ0]});Q5=makeQuery(id+"F0.imprint","IMPRINT",FACE,{"disambiguationData":[TD([[makeQuery(id+"F0.imprint","IMPRINT",EDGE,{"disambiguationData":[TD([[subQ2,1.0]])],"derivedFrom":subQ1}),-1.0]])]});}
            var Q6;
            Q6=sQuery(id+"F0.wireOp",EDGE,"E37");
            revolve(context, id + "F16", {"entities" : qUnion([Q0, Q1, Q2, Q3, Q4, Q5]), "axis" : qUnion([Q6]), "revolveType" : RevolveType.FULL});
        }
        {
            var Q0;
            Q0=makeQuery(id+"F0.imprint","IMPRINT",FACE,{"disambiguationData":[TD([[makeQuery(id+"F0.imprint","IMPRINT",EDGE,{"derivedFrom":sQuery(id+"F0.wireOp",EDGE,"E30")}),1.0]])]});
            var Q1;
            Q1=sQuery(id+"F0.wireOp",EDGE,"E63");
            revolve(context, id + "F17", {"entities" : qUnion([Q0]), "axis" : qUnion([Q1]), "revolveType" : RevolveType.FULL});
        }
        {
            var Q0;
            {var subQ0=sQuery(id+"F0.wireOp",EDGE,"E37");var subQ1=sQuery(id+"F0.wireOp",EDGE,"E29.4.12");var subQ2=makeQuery(id+"F0.imprint","INTERSECT",VERTEX,{"derivedFrom":[subQ1,subQ0]});Q0=makeQuery(id+"F0.imprint","IMPRINT",FACE,{"disambiguationData":[TD([[makeQuery(id+"F0.imprint","IMPRINT",EDGE,{"disambiguationData":[TD([[subQ2,-1.0]])],"derivedFrom":subQ0}),1.0]])]});}
            var Q1;
            {var subQ0=sQuery(id+"F0.wireOp",EDGE,"E66");var subQ1=sQuery(id+"F0.wireOp",EDGE,"E37");var subQ2=makeQuery(id+"F0.imprint","INTERSECT",VERTEX,{"derivedFrom":[subQ1,subQ0]});Q1=makeQuery(id+"F0.imprint","IMPRINT",FACE,{"disambiguationData":[TD([[makeQuery(id+"F0.imprint","IMPRINT",EDGE,{"disambiguationData":[TD([[subQ2,-1.0]])],"derivedFrom":subQ1}),1.0]])]});}
            var Q2;
            {var subQ0=sQuery(id+"F0.wireOp",EDGE,"E64");var subQ1=sQuery(id+"F0.wireOp",EDGE,"E37");var subQ2=makeQuery(id+"F0.imprint","INTERSECT",VERTEX,{"derivedFrom":[subQ1,subQ0]});Q2=makeQuery(id+"F0.imprint","IMPRINT",FACE,{"disambiguationData":[TD([[makeQuery(id+"F0.imprint","IMPRINT",EDGE,{"disambiguationData":[TD([[subQ2,1.0]])],"derivedFrom":subQ1}),1.0]])]});}
            var Q3;
            {var subQ0=sQuery(id+"F0.wireOp",EDGE,"E70");Q3=makeQuery(id+"F0.imprint","IMPRINT",FACE,{"disambiguationData":[TD([[makeQuery(id+"F0.imprint","IMPRINT",EDGE,{"derivedFrom":subQ0}),1.0]])]});}
            var Q4;
            {var subQ3=sQuery(id+"F0.wireOp",EDGE,"E37");var subQ5=sQuery(id+"F0.wireOp",EDGE,"E53");var subQ6=makeQuery(id+"F0.imprint","INTERSECT",VERTEX,{"derivedFrom":[subQ3,subQ5]});Q4=makeQuery(id+"F0.imprint","IMPRINT",FACE,{"disambiguationData":[TD([[makeQuery(id+"F0.imprint","IMPRINT",EDGE,{"disambiguationData":[TD([[subQ6,-1.0]])],"derivedFrom":subQ3}),1.0]])]});}
            var Q5;
            Q5=sQuery(id+"F0.wireOp",EDGE,"E37");
            revolve(context, id + "F18", {"operationType" : NewBodyOperationType.ADD, "entities" : qUnion([Q0, Q1, Q2, Q3, Q4]), "axis" : qUnion([Q5]), "revolveType" : RevolveType.FULL});
        }
        {
            var Q0;
            Q0=qCreatedBy(makeId("Right.planeOp"),FACE);
            var sketch = newSketch(context, id + "F19", { "sketchPlane" : qUnion([Q0])});
            skLineSegment(sketch, "E81.top", {"start": v(82.5, -15) * mm, "end": v(-92.5, -15) * mm});
            skLineSegment(sketch, "E82", {"start": v(-77.5, -10) * mm, "end": v(-77.5, 25) * mm});
            skLineSegment(sketch, "E83", {"start": v(-77.5, 25) * mm, "end": v(-92.5, 25) * mm});
            skLineSegment(sketch, "E84", {"start": v(-92.5, 25) * mm, "end": v(-92.5, -15) * mm});
            skPoint(sketch, "E85", {"position": v(-92.5, 15) * mm});
            skLineSegment(sketch, "E86", {"start": v(72.5, -10) * mm, "end": v(72.5, 25) * mm});
            skLineSegment(sketch, "E87", {"start": v(72.5, 25) * mm, "end": v(82.5, 25) * mm});
            skLineSegment(sketch, "E88", {"start": v(82.5, 25) * mm, "end": v(82.5, -15) * mm});
            skLineSegment(sketch, "E89.trimOffspring", {"start": v(72.5, -10) * mm, "end": v(-77.5, -10) * mm});
            skLineSegment(sketch, "E90.bottom", {"start": v(37.5, 20) * mm, "end": v(97.5, 20) * mm});
            skLineSegment(sketch, "E90.top", {"start": v(37.5, 15) * mm, "end": v(97.5, 15) * mm});
            skLineSegment(sketch, "E90.left", {"start": v(37.5, 20) * mm, "end": v(37.5, 15) * mm});
            skLineSegment(sketch, "E90.right", {"start": v(97.5, 20) * mm, "end": v(97.5, 15) * mm});
            skPoint(sketch, "E91", {"position": v(82.5, 15) * mm});
            skSolve(sketch);
        }
        {
            var Q0;
            {var subQ5=sQuery(id+"F19.wireOp",EDGE,"E90.left");Q0=makeQuery(id+"F19.imprint","IMPRINT",FACE,{"disambiguationData":[TD([[makeQuery(id+"F19.imprint","IMPRINT",EDGE,{"derivedFrom":subQ5}),1.0]])]});}
            var Q1;
            {var subQ0=sQuery(id+"F19.wireOp",EDGE,"E90.top");var subQ1=sQuery(id+"F19.wireOp",EDGE,"E86");var subQ2=makeQuery(id+"F19.imprint","INTERSECT",VERTEX,{"derivedFrom":[subQ1,subQ0]});Q1=makeQuery(id+"F19.imprint","IMPRINT",FACE,{"disambiguationData":[TD([[makeQuery(id+"F19.imprint","IMPRINT",EDGE,{"disambiguationData":[TD([[subQ2,-1.0]])],"derivedFrom":subQ1}),-1.0]])]});}
            var Q2;
            {var subQ5=sQuery(id+"F19.wireOp",EDGE,"E90.right");Q2=makeQuery(id+"F19.imprint","IMPRINT",FACE,{"disambiguationData":[TD([[makeQuery(id+"F19.imprint","IMPRINT",EDGE,{"derivedFrom":subQ5}),-1.0]])]});}
            var Q3;
            Q3=sQuery(id+"F19.wireOp",EDGE,"E90.top");
            revolve(context, id + "F20", {"operationType" : NewBodyOperationType.ADD, "entities" : qUnion([Q0, Q1, Q2]), "axis" : qUnion([Q3]), "revolveType" : RevolveType.FULL});
        }
        {
            var Q0;
            {var subQ0=sQuery(id+"F19.wireOp",EDGE,"E81.top");Q0=makeQuery(id+"F19.imprint","IMPRINT",FACE,{"disambiguationData":[TD([[makeQuery(id+"F19.imprint","IMPRINT",EDGE,{"derivedFrom":subQ0}),-1.0]])]});}
            var Q1;
            {var subQ0=sQuery(id+"F19.wireOp",EDGE,"E90.top");var subQ1=sQuery(id+"F19.wireOp",EDGE,"E86");var subQ2=makeQuery(id+"F19.imprint","INTERSECT",VERTEX,{"derivedFrom":[subQ1,subQ0]});Q1=makeQuery(id+"F19.imprint","IMPRINT",FACE,{"disambiguationData":[TD([[makeQuery(id+"F19.imprint","IMPRINT",EDGE,{"disambiguationData":[TD([[subQ2,-1.0]])],"derivedFrom":subQ1}),-1.0]])]});}
            var Q2;
            {var subQ0=sQuery(id+"F19.wireOp",EDGE,"E87");Q2=makeQuery(id+"F19.imprint","IMPRINT",FACE,{"disambiguationData":[TD([[makeQuery(id+"F19.imprint","IMPRINT",EDGE,{"derivedFrom":subQ0}),-1.0]])]});}
            extrude(context, id + "F21", {"entities" : qUnion([Q0, Q1, Q2]), "endBound" : BoundingType.SYMMETRIC, "depth" : 40 * mm, "offsetDistance" : 25 * mm});
        }
        {
            var Q0;
            Q0=makeQuery(id+"F21.opExtrude","SWEPT_FACE",FACE,{"disambiguationData":[OSD([sQuery(id+"F19.wireOp",EDGE,"E88")])]});
            var sketch = newSketch(context, id + "F22", { "sketchPlane" : qUnion([Q0])});
            skPoint(sketch, "E92", {"position": v(0, 15) * mm});
            skSolve(sketch);
        }
        {
            var Q0;
            Q0=sQuery(id+"F22.wireOp",VERTEX,"E92");
            var Q1;
            Q1=makeQuery(id+"F21.opExtrude","SWEPT_BODY",BODY,{"disambiguationData":[OSD([sQuery(id+"F19.wireOp",EDGE,"E81.top"),sQuery(id+"F19.wireOp",EDGE,"E82"),sQuery(id+"F19.wireOp",EDGE,"E83"),sQuery(id+"F19.wireOp",EDGE,"E84"),sQuery(id+"F19.wireOp",EDGE,"E86"),sQuery(id+"F19.wireOp",EDGE,"E87"),sQuery(id+"F19.wireOp",EDGE,"E88"),sQuery(id+"F19.wireOp",EDGE,"E89.trimOffspring")])]});
            hole(context, id + "F23", {"style" : HoleStyle.SIMPLE, "endStyle" : HoleEndStyle.BLIND, "holeDiameter" : 10.5 * mm, "majorDiameter" : 5 * mm, "holeDepth" : 10 * mm, "isTappedThrough" : true, "tappedDepth" : 12 * mm, "tapClearance" : 3, "locations" : qUnion([Q0]), "scope" : qUnion([Q1])});
        }
        {
            var Q0;
            Q0=makeQuery(id+"F21.opExtrude","SWEPT_FACE",FACE,{"disambiguationData":[OSD([sQuery(id+"F19.wireOp",EDGE,"E84")])]});
            var sketch = newSketch(context, id + "F24", { "sketchPlane" : qUnion([Q0])});
            skPoint(sketch, "E93", {"position": v(0, 15) * mm});
            skSolve(sketch);
        }
        {
            var Q0;
            Q0=sQuery(id+"F24.wireOp",VERTEX,"E93");
            var Q1;
            Q1=makeQuery(id+"F21.opExtrude","SWEPT_BODY",BODY,{"disambiguationData":[OSD([sQuery(id+"F19.wireOp",EDGE,"E81.top"),sQuery(id+"F19.wireOp",EDGE,"E82"),sQuery(id+"F19.wireOp",EDGE,"E83"),sQuery(id+"F19.wireOp",EDGE,"E84"),sQuery(id+"F19.wireOp",EDGE,"E86"),sQuery(id+"F19.wireOp",EDGE,"E87"),sQuery(id+"F19.wireOp",EDGE,"E88"),sQuery(id+"F19.wireOp",EDGE,"E89.trimOffspring")])]});
            hole(context, id + "F25", {"style" : HoleStyle.SIMPLE, "endStyle" : HoleEndStyle.BLIND, "holeDiameter" : 10.5 * mm, "majorDiameter" : 5 * mm, "holeDepth" : 30 * mm, "isTappedThrough" : true, "tappedDepth" : 12 * mm, "tapClearance" : 3, "locations" : qUnion([Q0]), "scope" : qUnion([Q1])});
        }
        {
            var Q0;
            Q0=makeQuery(id+"F21.opExtrude","SWEPT_FACE",FACE,{"disambiguationData":[OSD([sQuery(id+"F19.wireOp",EDGE,"E89.trimOffspring")])]});
            var sketch = newSketch(context, id + "F26", { "sketchPlane" : qUnion([Q0])});
            skLineSegment(sketch, "E94.bottom", {"start": v(-10, -67.5) * mm, "end": v(10, -67.5) * mm});
            skLineSegment(sketch, "E94.top", {"start": v(-10, 62.5) * mm, "end": v(10, 62.5) * mm});
            skLineSegment(sketch, "E94.left", {"start": v(-10, -67.5) * mm, "end": v(-10, 62.5) * mm});
            skLineSegment(sketch, "E94.right", {"start": v(10, -67.5) * mm, "end": v(10, 62.5) * mm});
            skSolve(sketch);
        }
        {
            var Q0;
            Q0=makeQuery(id+"F26.imprint","IMPRINT",FACE,{"disambiguationData":[TD([[makeQuery(id+"F26.imprint","IMPRINT",EDGE,{"derivedFrom":sQuery(id+"F26.wireOp",EDGE,"E94.bottom")}),1.0]])]});
            extrude(context, id + "F27", {"entities" : qUnion([Q0]), "operationType" : NewBodyOperationType.REMOVE, "endBound" : BoundingType.UP_TO_NEXT, "oppositeDirection" : true, "depth" : 25 * mm, "offsetDistance" : 25 * mm});
        }
        {
            var Q0;
            Q0=makeQuery(id+"F21.opExtrude","SWEPT_FACE",FACE,{"disambiguationData":[OSD([sQuery(id+"F19.wireOp",EDGE,"E84")])]});
            var sketch = newSketch(context, id + "F28", { "sketchPlane" : qUnion([Q0])});
            skLineSegment(sketch, "E95.bottom", {"start": v(-20, 25) * mm, "end": v(-10, 25) * mm});
            skLineSegment(sketch, "E95.top", {"start": v(-20, -10) * mm, "end": v(-10, -10) * mm});
            skLineSegment(sketch, "E95.left", {"start": v(-20, 25) * mm, "end": v(-20, -10) * mm});
            skLineSegment(sketch, "E95.right", {"start": v(-10, 25) * mm, "end": v(-10, -10) * mm});
            skLineSegment(sketch, "E96.MirrorCS", {"start": v(10, 25) * mm, "end": v(10, -10) * mm});
            skLineSegment(sketch, "E97.MirrorCS", {"start": v(20, 25) * mm, "end": v(10, 25) * mm});
            skLineSegment(sketch, "E98.MirrorCS", {"start": v(20, 25) * mm, "end": v(20, -10) * mm});
            skLineSegment(sketch, "E99.MirrorCS", {"start": v(20, -10) * mm, "end": v(10, -10) * mm});
            skSolve(sketch);
        }
        {
            var Q0;
            Q0=makeQuery(id+"F28.imprint","IMPRINT",FACE,{"disambiguationData":[TD([[makeQuery(id+"F28.imprint","IMPRINT",EDGE,{"derivedFrom":sQuery(id+"F28.wireOp",EDGE,"E95.bottom")}),1.0]])]});
            var Q1;
            Q1=makeQuery(id+"F28.imprint","IMPRINT",FACE,{"disambiguationData":[TD([[makeQuery(id+"F28.imprint","IMPRINT",EDGE,{"derivedFrom":sQuery(id+"F28.wireOp",EDGE,"E96.MirrorCS")}),1.0]])]});
            extrude(context, id + "F29", {"entities" : qUnion([Q0, Q1]), "operationType" : NewBodyOperationType.REMOVE, "endBound" : BoundingType.THROUGH_ALL, "oppositeDirection" : true, "depth" : 25 * mm, "offsetDistance" : 25 * mm});
        }
    });
